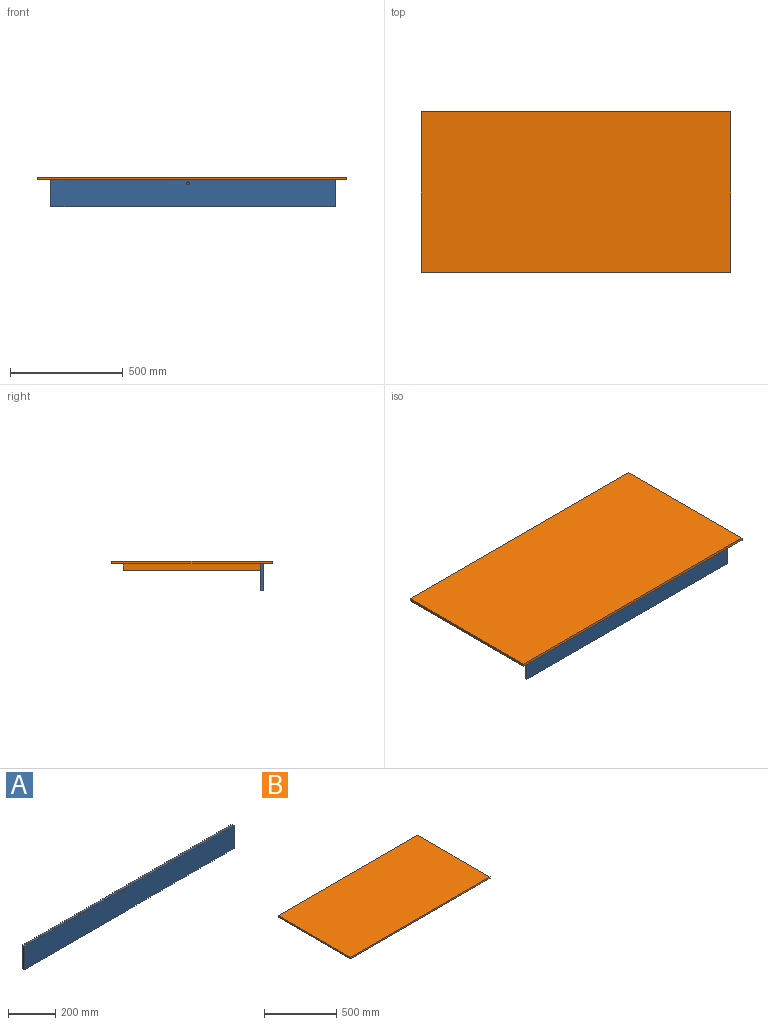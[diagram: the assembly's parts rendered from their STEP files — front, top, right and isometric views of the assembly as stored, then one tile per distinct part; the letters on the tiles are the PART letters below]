
ASSEMBLY  parts=2 mates=1
PART A: 8 faces, bbox 1260x12x120 mm
  f0: plane 1260x12mm, normal (0,0,1), area 15120mm2, adj f1,f3,f4,f5
  f1: plane 120x12mm, normal (-1,0,0), area 1440mm2, adj f0,f2,f4,f5
  f2: plane 1260x12mm, normal (0,0,-1), area 15120mm2, adj f1,f3,f4,f5
  f3: plane 120x12mm, normal (1,0,0), area 1440mm2, adj f0,f2,f4,f5
  f4: plane 1260x120mm, normal (0,-1,0), area 151200mm2, adj f0,f1,f2,f3
  f5: plane 1260x120mm, normal (0,1,0), area 151078.1mm2, adj f0,f1,f2,f3,f6
  f6: cylinder r=6.23mm len=12.46mm, axis (0,1,0), area 391.4mm2, adj f5,f7
  f7: plane 12.46x12.46mm, normal (0,1,0), area 121.9mm2, adj f6
PART B: 13 faces, bbox 1370x711x42 mm
  f0: plane 1370x12mm, normal (0,1,0), area 16440mm2, adj f1,f3,f4,f5
  f1: plane 711x12mm, normal (-1,0,0), area 8532mm2, adj f0,f2,f4,f5
  f2: plane 1370x12mm, normal (0,-1,0), area 16440mm2, adj f1,f3,f4,f5
  f3: plane 711x12mm, normal (1,0,0), area 8532mm2, adj f0,f2,f4,f5
  f4: plane 1370x711mm, normal (0,0,1), area 974070mm2, adj f0,f1,f2,f3
  f5: plane 1370x711mm, normal (0,0,-1), area 204210mm2, adj f0,f1,f2,f3,f6,f7,f8,f9
  f6: plane 1260x30mm, normal (0,-1,0), area 37510.9mm2, adj f5,f7,f9,f10,f11
  f7: plane 611x30mm, normal (-1,0,0), area 18330mm2, adj f5,f6,f8,f10
  f8: plane 1260x30mm, normal (0,1,0), area 37800mm2, adj f5,f7,f9,f10
  f9: plane 611x30mm, normal (1,0,0), area 18330mm2, adj f5,f6,f8,f10
  f10: plane 1260x611mm, normal (0,0,-1), area 769860mm2, adj f6,f7,f8,f9
  f11: cylinder r=9.59mm len=30mm, axis (0,-1,0), area 1808.3mm2, adj f6,f12
  f12: plane 19.19x19.19mm, normal (0,-1,0), area 289.1mm2, adj f11
PLACE A t=(-19.2,-266.89,-33.67)mm
PLACE B at identity
MATE planar A.f5 <-> B.f6  axis (0,1,0) through (-626.91,-266.89,0)mm
